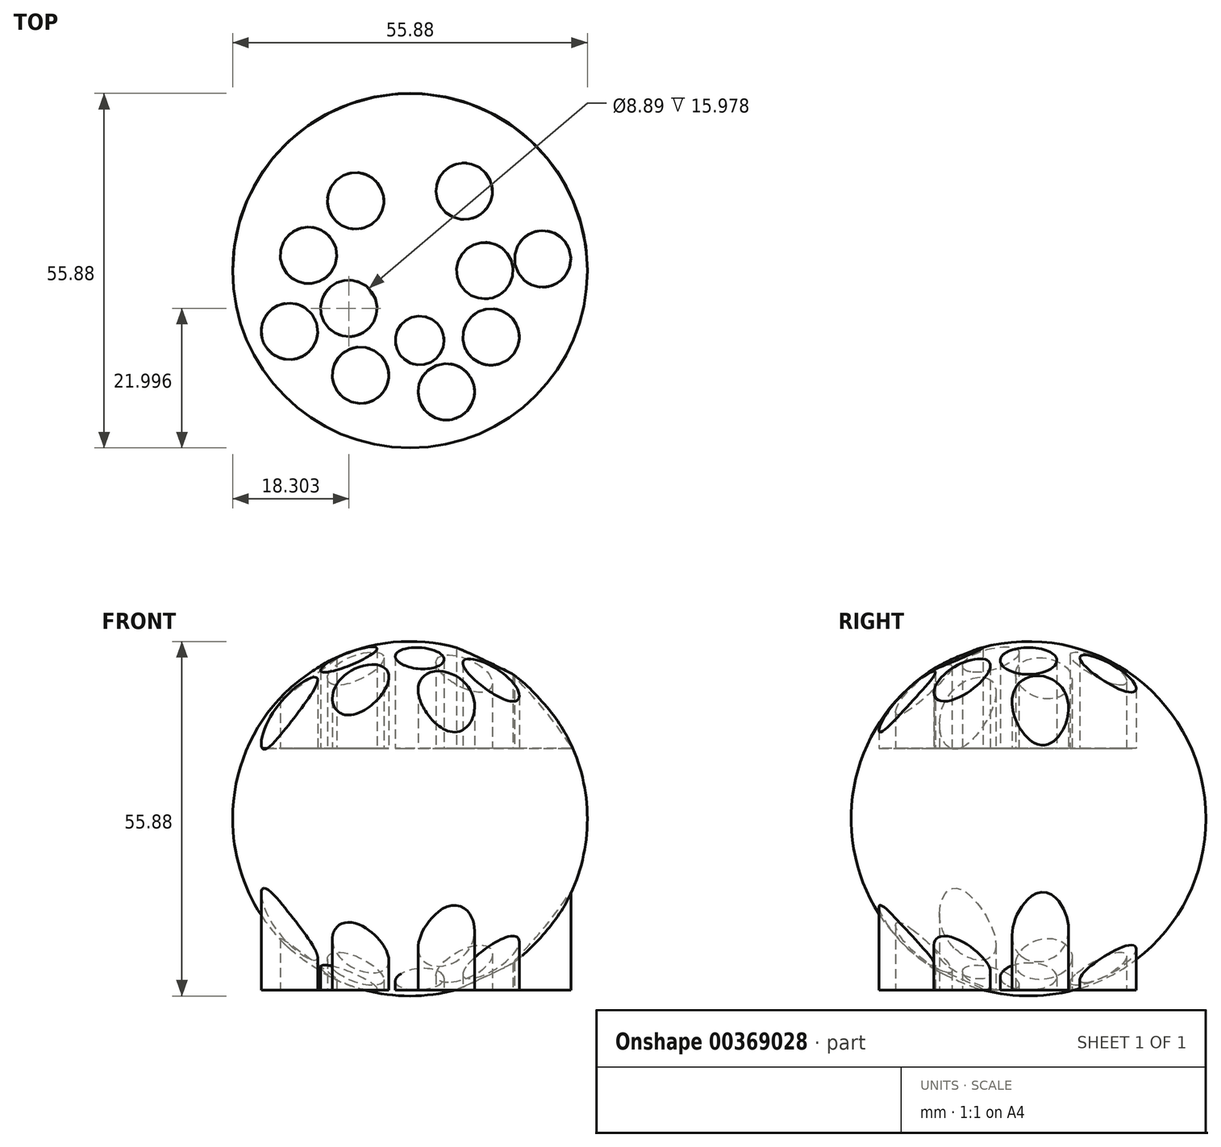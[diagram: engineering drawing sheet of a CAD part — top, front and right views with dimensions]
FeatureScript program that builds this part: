
annotation { "Feature Type Name" : "Feature", "Feature Type Description" : "" }
export const myFeature = defineFeature(function(context is Context, id is Id, definition is map)
    precondition{}
    {
        {
            var Q0;
            Q0=qCreatedBy(makeId("Front.planeOp"),FACE);
            var sketch = newSketch(context, id + "F0", { "sketchPlane" : qUnion([Q0])});
            skLineSegment(sketch, "E0", {"start": v(-36.48, 27) * mm, "end": v(19.4, 27) * mm});
            skArc(sketch, "E1", {"start": v(19.4, 27) * mm, "mid": v(-8.54, 54.93) * mm, "end": v(-36.48, 27) * mm});
            skLineSegment(sketch, "E2", {"start": v(-36.48, 27) * mm, "end": v(-8.54, 27) * mm});
            skLineSegment(sketch, "E3", {"start": v(-8.54, 54.93) * mm, "end": v(-8.54, 27) * mm});
            skSolve(sketch);
        }
        {
            var Q0;
            {var subQ3=sQuery(id+"F0.wireOp",EDGE,"E3");Q0=makeQuery(id+"F0.imprint","IMPRINT",FACE,{"disambiguationData":[TD([[makeQuery(id+"F0.imprint","IMPRINT",EDGE,{"derivedFrom":subQ3}),-1.0]])]});}
            var Q1;
            {var subQ3=sQuery(id+"F0.wireOp",EDGE,"E3");Q1=makeQuery(id+"F0.imprint","IMPRINT",FACE,{"disambiguationData":[TD([[makeQuery(id+"F0.imprint","IMPRINT",EDGE,{"derivedFrom":subQ3}),1.0]])]});}
            var Q2;
            Q2=sQuery(id+"F0.wireOp",EDGE,"E0");
            revolve(context, id + "F1", {"entities" : qUnion([Q0, Q1]), "axis" : qUnion([Q2]), "revolveType" : RevolveType.FULL});
        }
        {
            var Q0;
            Q0=qCreatedBy(makeId("Top.planeOp"),FACE);
            var sketch = newSketch(context, id + "F2", { "sketchPlane" : qUnion([Q0])});
            skCircle(sketch, "E4", {"center": v(3.24, 0) * mm, "radius": 4.45 * mm});
            skCircle(sketch, "E5", {"center": v(-27.53, -9.58) * mm, "radius": 4.45 * mm});
            skCircle(sketch, "E6", {"center": v(-16.33, -16.48) * mm, "radius": 4.45 * mm});
            skCircle(sketch, "E7", {"center": v(-24.53, 2.41) * mm, "radius": 4.45 * mm});
            skCircle(sketch, "E8", {"center": v(-17.1, 11) * mm, "radius": 4.45 * mm});
            skCircle(sketch, "E9", {"center": v(0, 12.52) * mm, "radius": 4.45 * mm});
            skCircle(sketch, "E10", {"center": v(-18.18, -5.94) * mm, "radius": 4.45 * mm});
            skCircle(sketch, "E11", {"center": v(4.22, -10.45) * mm, "radius": 4.45 * mm});
            skCircle(sketch, "E12", {"center": v(12.35, 1.85) * mm, "radius": 4.45 * mm});
            skCircle(sketch, "E13", {"center": v(-7.02, -11) * mm, "radius": 3.84 * mm});
            skCircle(sketch, "E14", {"center": v(-2.81, -19.1) * mm, "radius": 4.45 * mm});
            skSolve(sketch);
        }
        {
            var Q0;
            Q0 = qSketchRegion(id + "F2", true);
            extrude(context, id + "F3", {"entities" : qUnion([Q0]), "operationType" : NewBodyOperationType.REMOVE, "depth" : 101.6 * mm});
        }
        {
            var Q0;
            Q0=makeQuery(id+"F2.imprint","IMPRINT",FACE,{"disambiguationData":[TD([[makeQuery(id+"F2.imprint","IMPRINT",EDGE,{"derivedFrom":sQuery(id+"F2.wireOp",EDGE,"E4")}),1.0]])]});
            var Q1;
            Q1=makeQuery(id+"F2.imprint","IMPRINT",FACE,{"disambiguationData":[TD([[makeQuery(id+"F2.imprint","IMPRINT",EDGE,{"derivedFrom":sQuery(id+"F2.wireOp",EDGE,"E5")}),1.0]])]});
            var Q2;
            Q2=makeQuery(id+"F2.imprint","IMPRINT",FACE,{"disambiguationData":[TD([[makeQuery(id+"F2.imprint","IMPRINT",EDGE,{"derivedFrom":sQuery(id+"F2.wireOp",EDGE,"E6")}),1.0]])]});
            var Q3;
            Q3=makeQuery(id+"F2.imprint","IMPRINT",FACE,{"disambiguationData":[TD([[makeQuery(id+"F2.imprint","IMPRINT",EDGE,{"derivedFrom":sQuery(id+"F2.wireOp",EDGE,"E7")}),1.0]])]});
            var Q4;
            Q4=makeQuery(id+"F2.imprint","IMPRINT",FACE,{"disambiguationData":[TD([[makeQuery(id+"F2.imprint","IMPRINT",EDGE,{"derivedFrom":sQuery(id+"F2.wireOp",EDGE,"E8")}),1.0]])]});
            var Q5;
            Q5=makeQuery(id+"F2.imprint","IMPRINT",FACE,{"disambiguationData":[TD([[makeQuery(id+"F2.imprint","IMPRINT",EDGE,{"derivedFrom":sQuery(id+"F2.wireOp",EDGE,"E9")}),1.0]])]});
            var Q6;
            Q6=makeQuery(id+"F2.imprint","IMPRINT",FACE,{"disambiguationData":[TD([[makeQuery(id+"F2.imprint","IMPRINT",EDGE,{"derivedFrom":sQuery(id+"F2.wireOp",EDGE,"E11")}),1.0]])]});
            var Q7;
            Q7=makeQuery(id+"F2.imprint","IMPRINT",FACE,{"disambiguationData":[TD([[makeQuery(id+"F2.imprint","IMPRINT",EDGE,{"derivedFrom":sQuery(id+"F2.wireOp",EDGE,"E12")}),1.0]])]});
            var Q8;
            Q8=makeQuery(id+"F2.imprint","IMPRINT",FACE,{"disambiguationData":[TD([[makeQuery(id+"F2.imprint","IMPRINT",EDGE,{"derivedFrom":sQuery(id+"F2.wireOp",EDGE,"E14")}),1.0]])]});
            var Q9;
            Q9=makeQuery(id+"F2.imprint","IMPRINT",FACE,{"disambiguationData":[TD([[makeQuery(id+"F2.imprint","IMPRINT",EDGE,{"derivedFrom":sQuery(id+"F2.wireOp",EDGE,"E10")}),1.0]])]});
            var Q10;
            Q10=makeQuery(id+"F2.imprint","IMPRINT",FACE,{"disambiguationData":[TD([[makeQuery(id+"F2.imprint","IMPRINT",EDGE,{"derivedFrom":sQuery(id+"F2.wireOp",EDGE,"E13")}),1.0]])]});
            extrude(context, id + "F4", {"entities" : qUnion([Q0, Q1, Q2, Q3, Q4, Q5, Q6, Q7, Q8, Q9, Q10]), "operationType" : NewBodyOperationType.ADD, "depth" : 38.1 * mm});
        }
    });
